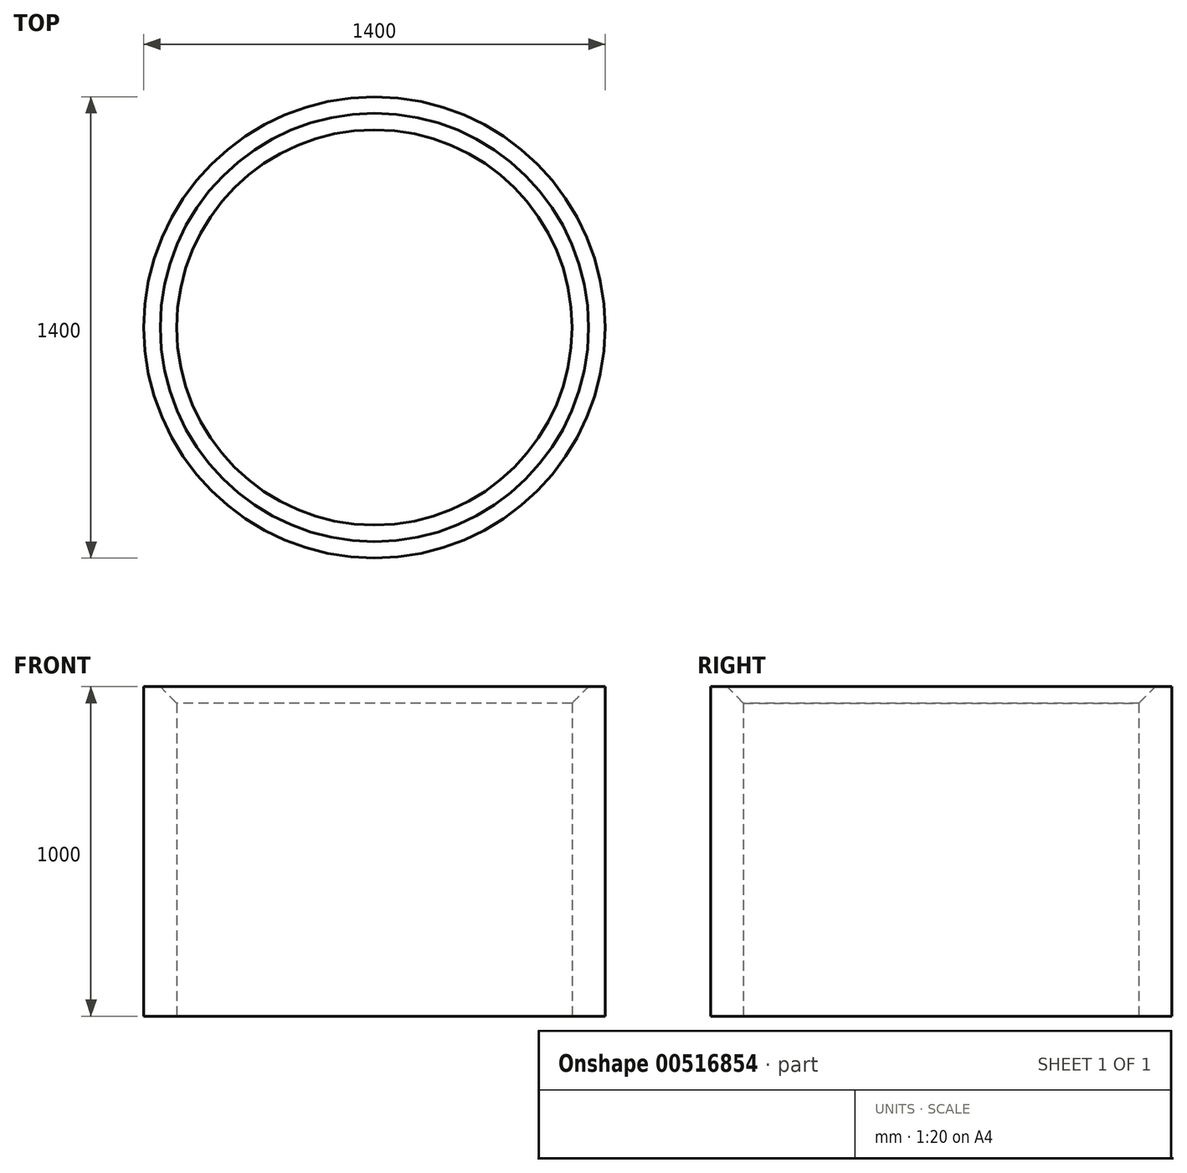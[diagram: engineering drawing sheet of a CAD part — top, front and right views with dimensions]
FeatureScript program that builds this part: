
annotation { "Feature Type Name" : "Feature", "Feature Type Description" : "" }
export const myFeature = defineFeature(function(context is Context, id is Id, definition is map)
    precondition{}
    {
        {
            var Q0;
            Q0=qCreatedBy(makeId("Top.planeOp"),FACE);
            var sketch = newSketch(context, id + "F0", { "sketchPlane" : qUnion([Q0])});
            skCircle(sketch, "E0", {"center": v(0, 0) * mm, "radius": 700 * mm});
            skCircle(sketch, "E1", {"center": v(0, 0) * mm, "radius": 600 * mm});
            skSolve(sketch);
        }
        {
            var Q0;
            Q0=makeQuery(id+"F0.imprint","IMPRINT",FACE,{"disambiguationData":[TD([[makeQuery(id+"F0.imprint","IMPRINT",EDGE,{"derivedFrom":sQuery(id+"F0.wireOp",EDGE,"E0")}),1.0]])]});
            extrude(context, id + "F1", {"entities" : qUnion([Q0]), "endBound" : BoundingType.SYMMETRIC, "depth" : 1000 * mm});
        }
        {
            var Q0;
            Q0=makeQuery(id+"F1.opExtrude","CAP_EDGE",EDGE,{"disambiguationData":[OSD([sQuery(id+"F0.wireOp",EDGE,"E1")])],"isStart":false});
            chamfer(context, id + "F2", {"entities" : qUnion([Q0]), "width" : 50 * mm, "tangentPropagation" : true});
        }
    });
